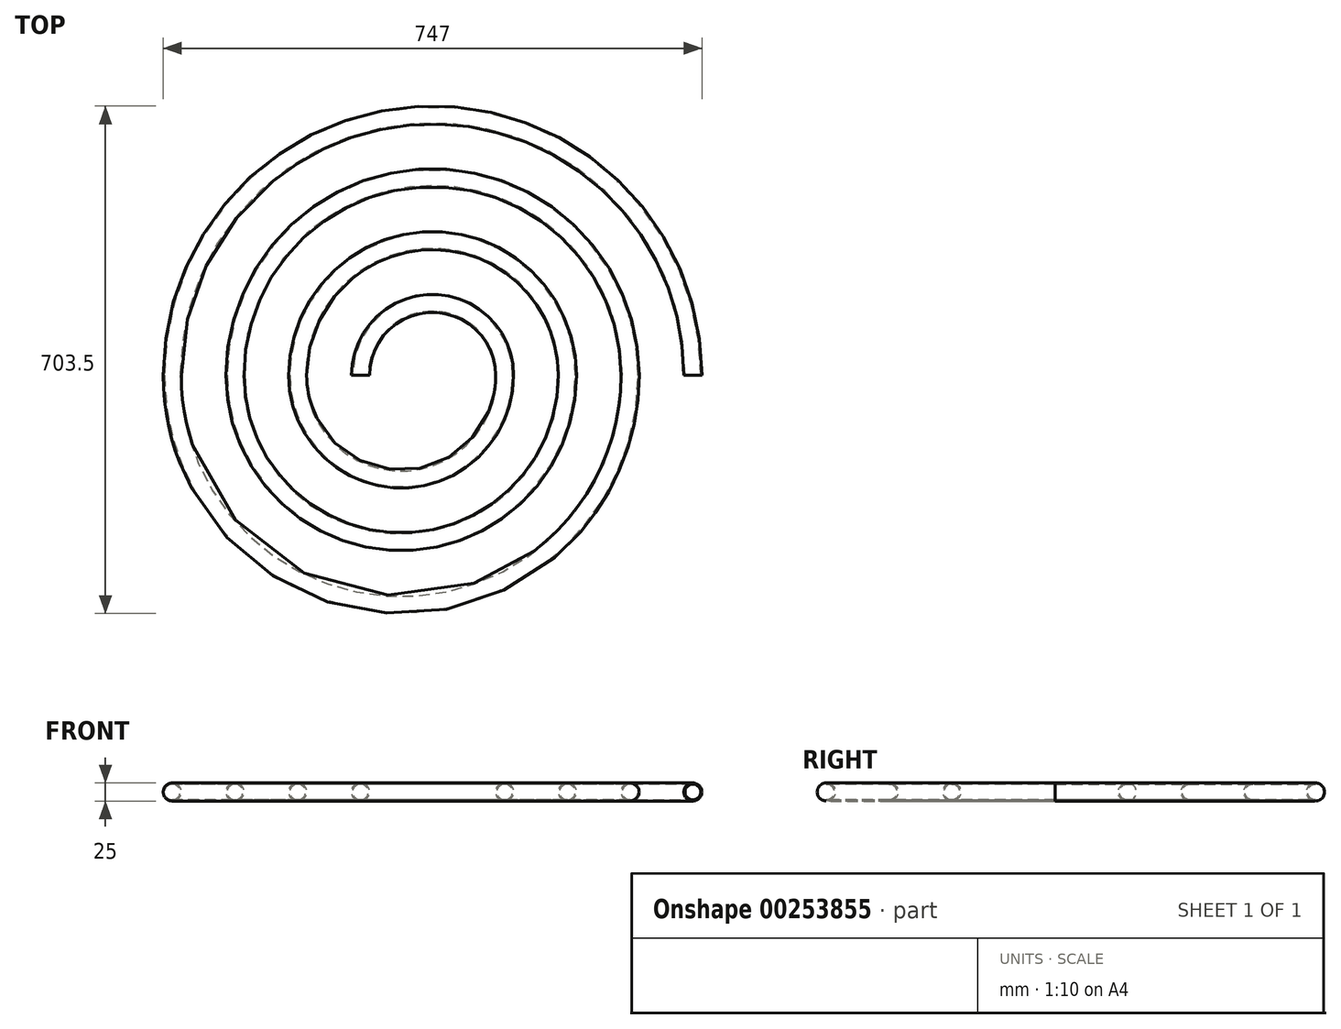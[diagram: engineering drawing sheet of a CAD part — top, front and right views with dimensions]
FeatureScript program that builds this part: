
annotation { "Feature Type Name" : "Feature", "Feature Type Description" : "" }
export const myFeature = defineFeature(function(context is Context, id is Id, definition is map)
    precondition{}
    {
        {
            var Q0;
            Q0=qCreatedBy(makeId("Top.planeOp"),FACE);
            var sketch = newSketch(context, id + "F0", { "sketchPlane" : qUnion([Q0])});
            skArc(sketch, "E0", {"start": v(100, 0) * mm, "mid": v(0, 100) * mm, "end": v(-100, 0) * mm});
            skArc(sketch, "E1", {"start": v(-187, 0) * mm, "mid": v(-43.5, -143.5) * mm, "end": v(100, 0) * mm});
            skArc(sketch, "E2", {"start": v(187, 0) * mm, "mid": v(0, 187) * mm, "end": v(-187, 0) * mm});
            skArc(sketch, "E3", {"start": v(-274, 0) * mm, "mid": v(-43.5, -230.5) * mm, "end": v(187, 0) * mm});
            skArc(sketch, "E4", {"start": v(274, 0) * mm, "mid": v(0, 274) * mm, "end": v(-274, 0) * mm});
            skArc(sketch, "E5", {"start": v(-361, 0) * mm, "mid": v(-43.5, -317.5) * mm, "end": v(274, 0) * mm});
            skArc(sketch, "E6", {"start": v(361, 0) * mm, "mid": v(0, 361) * mm, "end": v(-361, 0) * mm});
            skSolve(sketch);
        }
        {
            var Q0;
            Q0=qCreatedBy(makeId("Front.planeOp"),FACE);
            var sketch = newSketch(context, id + "F1", { "sketchPlane" : qUnion([Q0])});
            skPoint(sketch, "E7.0", {"position": v(-100, 0) * mm});
            skCircle(sketch, "E8", {"center": v(-100, 0) * mm, "radius": 12.5 * mm});
            skCircle(sketch, "E9.0", {"center": v(-100, 0) * mm, "radius": 11 * mm});
            skPoint(sketch, "E10", {"position": v(-115, 0) * mm});
            skPoint(sketch, "E11.0", {"position": v(-187, 0) * mm});
            skCircle(sketch, "E12", {"center": v(-187, 0) * mm, "radius": 12.5 * mm});
            skPoint(sketch, "E13", {"position": v(-172, 0) * mm});
            skLineSegment(sketch, "E14.bottom", {"start": v(-172, 14.5) * mm, "end": v(-171, 14.5) * mm});
            skLineSegment(sketch, "E14.top", {"start": v(-172, -14.5) * mm, "end": v(-171, -14.5) * mm});
            skLineSegment(sketch, "E14.left", {"start": v(-172, 14.5) * mm, "end": v(-172, -14.5) * mm});
            skLineSegment(sketch, "E14.right", {"start": v(-171, 14.5) * mm, "end": v(-171, -14.5) * mm});
            skPoint(sketch, "E14.middle", {"position": v(-171.5, 0) * mm});
            skLineSegment(sketch, "E15.bottom", {"start": v(-115, 14.5) * mm, "end": v(-116, 14.5) * mm});
            skLineSegment(sketch, "E15.top", {"start": v(-115, -14.5) * mm, "end": v(-116, -14.5) * mm});
            skLineSegment(sketch, "E15.left", {"start": v(-115, 14.5) * mm, "end": v(-115, -14.5) * mm});
            skLineSegment(sketch, "E15.right", {"start": v(-116, 14.5) * mm, "end": v(-116, -14.5) * mm});
            skPoint(sketch, "E15.middle", {"position": v(-115.5, 0) * mm});
            skLineSegment(sketch, "E16.bottom", {"start": v(-171, 14.5) * mm, "end": v(-116, 14.5) * mm});
            skLineSegment(sketch, "E16.top", {"start": v(-171, -14.5) * mm, "end": v(-116, -14.5) * mm});
            skSolve(sketch);
        }
        {
            var Q0;
            Q0=makeQuery(id+"F1.imprint","IMPRINT",FACE,{"disambiguationData":[TD([[makeQuery(id+"F1.imprint","IMPRINT",EDGE,{"derivedFrom":sQuery(id+"F1.wireOp",EDGE,"E8")}),1.0]])]});
            var Q1;
            Q1=sQuery(id+"F0.wireOp",EDGE,"E0");
            var Q2;
            Q2=sQuery(id+"F0.wireOp",EDGE,"E1");
            var Q3;
            Q3=sQuery(id+"F0.wireOp",EDGE,"E2");
            var Q4;
            Q4=sQuery(id+"F0.wireOp",EDGE,"E3");
            var Q5;
            Q5=sQuery(id+"F0.wireOp",EDGE,"E4");
            var Q6;
            Q6=sQuery(id+"F0.wireOp",EDGE,"E5");
            var Q7;
            Q7=sQuery(id+"F0.wireOp",EDGE,"E6");
            sweep(context, id + "F2", {"profiles" : qUnion([Q0]), "path" : qUnion([Q1, Q2, Q3, Q4, Q5, Q6, Q7])});
        }
    });
